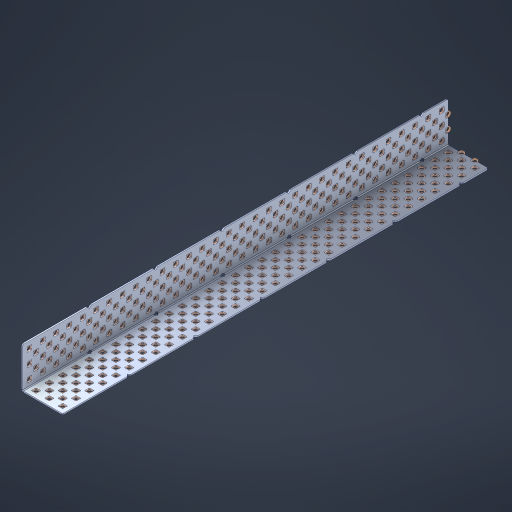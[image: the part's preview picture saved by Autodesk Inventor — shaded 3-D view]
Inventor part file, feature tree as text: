
AUTODESK INVENTOR PART (.ipt)
format: ipt  version: 2023 (Build 270158000, 158)  size: 3,180,544 bytes
history: native  units: in
note: dims shown in document units (in); Inventor stores cm internally (conversion verified against a paired STEP export)
features: other x326, extrude x318, sheet_metal_op x8, sketch x7, pattern_linear x3, mirror x1, chamfer x1
ambient origin geometry x8: Origin, YZ Plane, XZ Plane, XY Plane, X Axis, Y Axis, Z Axis, Center Point
bodies: Solid1 (feature_tree), Body (feature_tree)
feature tree (664):
  sheet_metal_op  "Flanges"
  sheet_metal_op  "Body Pattern"
  pattern_linear  "Center Double"  Spacing1=1.5in  [1 undecoded]
  pattern_linear  "Center Pattern"  Spacing1=0.1875in  [1 undecoded]
  other  "Arc Length"
  pattern_linear  "Notch Pattern"  Spacing1=0.0469in  [1 undecoded]
  other  "Diagonal Plane"
  mirror  "Everything Mirrored"
  chamfer  "End Chamfer"
  sketch  "Sketch1"  dims[d0=1.5in]
  other  "Plate1"
  sketch  "Sketch2"  dims[d1=16.0in]
  other  "Plate2"
  sheet_metal_op  "Bend1"
  sheet_metal_op  "Corner1"
  sketch  "Sketch8"  dims[d2=0.0469in]
  sketch  "Sketch9"  dims[d3=0.0469in]
  other  "Srf91"
  sheet_metal_op  "Body Pattern Sketch"
  other  "Srf92"
  sketch  "Sketch13"  dims[d4=0.0234in]
  sketch  "Sketch15"  dims[d5=0.0938in]
  sketch  "Sketch16"  dims[d6=0.0469in d7=1.5in d8=90.0deg d9=0.0312in d10=0.1875in d11=0.0469in d12=0.0469in d49=0.182in d50=0.02in d52=0.25in d53=0.0469in d54=0.0in d55=0.172in d56=1.0in d57=0.0in d85=0.1473in d86=0.1659in d89=0.0469in d90=0.0in d91=0.04in d92=0.0491in d95=2.5in d96=0.04in d97=0.25in d98=45.0deg d106=0.182in d107=0.02in d110=0.0469in d111=0.0in d112=0.172in d113=0.5in d114=0.0in d117=0.5in d126=0.0491in d127=0.1227in d128=0.08in d129=0.04in d130=2.5in d131=0.25in d132=12.5984in d134=0.5in d135=1.1811in d137=0.5in d140=0.5in d141=1.0in d142=0.3937in d144=0.5in d145=0.071in d146=0.7874in d148=0.5in]
  other  "Srf786"
  other  "Srf856"
  other  "Srf889"
  other  "Srf890"
  other  "Srf891"
  other  "Srf1275"
  other  "Srf1276"
  other  "Srf1278"
  other  "Srf1277"
  other  "Srf1285"
  other  "Srf1286"
  other  "Srf1287"
  other  "Srf1445"
  other  "Srf1446"
  other  "Srf1447"
  other  "Srf1448"
  other  "Srf1449"
  other  "Srf1537"
  other  "Srf1538"
  other  "Srf1539"
  other  "Srf1540"
  other  "Srf1541"
  other  "Srf1807"
  other  "Srf1808"
  other  "Srf1809"
  other  "Srf1810"
  other  "Srf1811"
  other  "Srf1812"
  other  "Srf1813"
  other  "Srf1814"
  other  "Srf1815"
  other  "Srf1816"
  other  "Srf1817"
  other  "Srf1818"
  other  "Srf1819"
  other  "Srf1820"
  other  "Srf1821"
  other  "Srf1822"
  other  "Srf1823"
  other  "Srf1824"
  other  "Srf1825"
  other  "Srf1826"
  other  "Srf1827"
  other  "Srf1828"
  other  "Srf1829"
  other  "Srf1959"
  other  "Srf1960"
  other  "Srf1961"
  other  "Srf1962"
  other  "Srf1963"
  other  "Srf1964"
  other  "Srf1965"
  other  "Srf1966"
  other  "Srf1967"
  other  "Srf1968"
  other  "Srf1969"
  other  "Srf1970"
  other  "Srf1971"
  other  "Srf1972"
  other  "Srf1973"
  other  "Srf1974"
  other  "Srf1975"
  other  "Srf1976"
  other  "Srf1977"
  other  "Srf1978"
  other  "Srf1979"
  other  "Srf1980"
  other  "Srf1981"
  other  "Srf2009"
  other  "Srf2010"
  other  "Srf2011"
  other  "Srf2012"
  other  "Srf2013"
  other  "Srf2014"
  other  "Srf2015"
  other  "Srf2016"
  other  "Srf2017"
  other  "Srf2018"
  other  "Srf2019"
  other  "Srf2020"
  other  "Srf2021"
  other  "Srf2022"
  other  "Srf2023"
  other  "Srf2024"
  other  "Srf2025"
  other  "Srf2026"
  other  "Srf2027"
  other  "Srf2028"
  other  "Srf2029"
  other  "Srf2030"
  other  "Srf2031"
  other  "Srf2032"
  other  "Srf2033"
  other  "Srf2034"
  other  "Srf2035"
  other  "Srf2036"
  other  "Srf2037"
  other  "Srf2038"
  other  "Srf2039"
  other  "Srf2040"
  other  "Srf2043"
  other  "Srf2044"
  other  "Srf2045"
  other  "Srf2046"
  other  "Srf2047"
  other  "Srf2048"
  other  "Srf2049"
  other  "Srf2050"
  other  "Srf2051"
  other  "Srf2052"
  other  "Srf2053"
  other  "Srf2054"
  other  "Srf2055"
  other  "Srf2056"
  other  "Srf2057"
  other  "Srf2058"
  other  "Srf2059"
  other  "Srf2060"
  other  "Srf2061"
  other  "Srf2062"
  other  "Srf2063"
  other  "Srf2064"
  other  "Srf2065"
  other  "Srf2066"
  other  "Srf2067"
  other  "Srf2068"
  other  "Srf2069"
  other  "Srf2070"
  other  "Srf2071"
  other  "Srf2072"
  other  "Srf2073"
  other  "Srf2076"
  other  "Srf2077"
  other  "Srf2078"
  other  "Srf2079"
  other  "Srf2080"
  other  "Srf2081"
  other  "Srf2082"
  other  "Srf2083"
  other  "Srf2084"
  other  "Srf2085"
  other  "Srf2086"
  other  "Srf2087"
  other  "Srf2088"
  other  "Srf2089"
  other  "Srf2090"
  other  "Srf2091"
  other  "Srf2092"
  other  "Srf2093"
  other  "Srf2094"
  other  "Srf2095"
  other  "Srf2096"
  other  "Srf2097"
  other  "Srf2098"
  other  "Srf2099"
  other  "Srf2100"
  other  "Srf2101"
  other  "Srf2102"
  other  "Srf2103"
  other  "Srf2104"
  other  "Srf2105"
  other  "Srf2106"
  other  "Srf2107"
  other  "Srf2108"
  other  "Srf2109"
  other  "Srf2110"
  other  "Srf2111"
  other  "Srf2112"
  other  "Srf2113"
  other  "Srf2114"
  other  "Srf2115"
  other  "Srf2116"
  other  "Srf2117"
  other  "Srf2118"
  other  "Srf2119"
  other  "Srf2120"
  other  "Srf2121"
  other  "Srf2122"
  other  "Srf2123"
  other  "Srf2124"
  other  "Srf2125"
  other  "Srf2126"
  other  "Srf2127"
  other  "Srf2128"
  other  "Srf2129"
  other  "Srf2130"
  other  "Srf2131"
  other  "Srf2132"
  other  "Srf2133"
  other  "Srf2134"
  other  "Srf2135"
  other  "Srf2136"
  other  "Srf2137"
  other  "Srf2138"
  other  "Srf2139"
  other  "Srf2140"
  other  "Srf2141"
  other  "Srf2142"
  other  "Srf2143"
  other  "Srf2144"
  other  "Srf2145"
  other  "Srf2146"
  other  "Srf2147"
  other  "Srf2148"
  other  "Srf2149"
  other  "Srf2150"
  other  "Srf2151"
  other  "Srf2152"
  other  "Srf2153"
  other  "Srf2154"
  other  "Srf2155"
  other  "Srf2156"
  other  "Srf2157"
  other  "Srf2158"
  other  "Srf2159"
  other  "Srf2160"
  other  "Srf2161"
  other  "Srf2162"
  other  "Srf2163"
  other  "Srf2164"
  other  "Srf2165"
  other  "Srf2166"
  other  "Srf2167"
  other  "Srf2168"
  other  "Srf2169"
  other  "Srf2179"
  other  "Srf2180"
  other  "Srf2181"
  other  "Srf2182"
  other  "Srf2183"
  other  "Srf2184"
  other  "Srf2185"
  other  "Srf2186"
  other  "Srf2187"
  other  "Srf2188"
  other  "Srf2189"
  other  "Srf2190"
  other  "Srf2191"
  other  "Srf2192"
  other  "Srf2193"
  other  "Srf2194"
  other  "Srf2195"
  other  "Srf2196"
  other  "Srf2197"
  other  "Srf2198"
  other  "Srf2199"
  other  "Srf2200"
  other  "Srf2201"
  other  "Srf2202"
  other  "Srf2203"
  other  "Srf2204"
  other  "Srf2205"
  other  "Srf2206"
  other  "Srf2207"
  other  "Srf2208"
  other  "Srf2209"
  other  "Srf2210"
  other  "Srf2211"
  other  "Srf2212"
  other  "Srf2213"
  other  "Srf2214"
  other  "Srf2215"
  other  "Srf2216"
  other  "Srf2217"
  other  "Srf2218"
  other  "Srf2219"
  other  "Srf2220"
  other  "Srf2221"
  other  "Srf2222"
  other  "Srf2223"
  other  "Srf2224"
  other  "Srf2225"
  other  "Srf2226"
  other  "Srf2227"
  other  "Srf2228"
  other  "Srf2229"
  other  "Srf2230"
  other  "Srf2231"
  other  "Srf2232"
  other  "Srf2233"
  other  "Srf2234"
  other  "Srf2235"
  other  "Srf2236"
  other  "Srf2237"
  other  "Srf2238"
  other  "Srf2239"
  other  "Srf2240"
  other  "Srf2241"
  other  "Srf2242"
  other  "Srf2243"
  other  "Srf2244"
  other  "Srf2245"
  other  "Srf2246"
  other  "Srf2247"
  other  "Srf2248"
  other  "Srf2249"
  other  "Srf2250"
  other  "Srf2251"
  other  "Srf2252"
  other  "Srf2253"
  other  "Srf2254"
  other  "Srf2255"
  other  "Srf2256"
  other  "Srf2257"
  other  "Srf2258"
  other  "Srf2259"
  other  "Srf2260"
  other  "Srf2261"
  other  "Srf2262"
  other  "Srf2263"
  other  "Srf2264"
  other  "Srf2265"
  other  "Srf2266"
  other  "Srf2267"
  other  "Srf2268"
  other  "Srf2269"
  other  "Srf2270"
  other  "Srf2271"
  sheet_metal_op  "Body Stamp"
  sheet_metal_op  "Body Circle"
  other  "Center Stamp"
  other  "Center Circle"
  sheet_metal_op  "Notch"
  extrude  "ExtrusionSrf92"  Depth=0.0469in
  extrude  "ExtrusionSrf856"  Depth=0.182in
  extrude  "ExtrusionSrf889"  Depth=0.02in
  extrude  "ExtrusionSrf890"  Depth=0.25in
  extrude  "ExtrusionSrf891"  Depth=0.0469in
  extrude  "ExtrusionSrf1275"  TaperAngle=0.0deg  [1 undecoded]
  extrude  "ExtrusionSrf1276"  Depth=0.5in
  extrude  "ExtrusionSrf1277"  Depth=1.0in TaperAngle=0.0deg
  extrude  "ExtrusionSrf1345"  Depth=0.5in
  extrude  "ExtrusionSrf1346"  Depth=0.5in
  extrude  "ExtrusionSrf1347"  Depth=0.0469in
  extrude  "ExtrusionSrf1348"  Depth=0.5in TaperAngle=0.0deg
  extrude  "ExtrusionSrf1445"  Depth=0.5in
  extrude  "ExtrusionSrf1446"  Depth=0.25in TaperAngle=45.0deg
  extrude  "ExtrusionSrf1447"  Depth=0.182in
  extrude  "ExtrusionSrf1448"  Depth=0.02in
  extrude  "ExtrusionSrf1449"  Depth=0.0469in
  extrude  "ExtrusionSrf1537"  TaperAngle=0.0deg  [1 undecoded]
  extrude  "ExtrusionSrf1538"  Depth=0.5in
  extrude  "ExtrusionSrf1539"  Depth=0.5in TaperAngle=0.0deg
  extrude  "ExtrusionSrf1540"  Depth=0.5in
  extrude  "ExtrusionSrf1541"  Depth=0.5in
  extrude  "ExtrusionSrf1807"  Depth=0.5in
  extrude  "ExtrusionSrf1808"  Depth=0.5in
  extrude  "ExtrusionSrf1809"  Depth=0.5in
  extrude  "ExtrusionSrf1810"  Depth=0.5in
  extrude  "ExtrusionSrf1811"  Depth=0.25in
  extrude  "ExtrusionSrf1812"  Depth=0.5in
  extrude  "ExtrusionSrf1813"  Depth=0.5in
  extrude  "ExtrusionSrf1814"  Depth=0.5in
  extrude  "ExtrusionSrf1815"  Depth=1.0in
  extrude  "ExtrusionSrf1816"  Depth=0.3937in
  extrude  "ExtrusionSrf1817"  Depth=0.5in
  extrude  "ExtrusionSrf1818"  Depth=0.5in
  extrude  "ExtrusionSrf1819"  [1 undecoded]
  extrude  "ExtrusionSrf1820"  [1 undecoded]
  extrude  "ExtrusionSrf1821"  [1 undecoded]
  extrude  "ExtrusionSrf1822"  [1 undecoded]
  extrude  "ExtrusionSrf1823"  [1 undecoded]
  extrude  "ExtrusionSrf1824"  [1 undecoded]
  extrude  "ExtrusionSrf1825"  [1 undecoded]
  extrude  "ExtrusionSrf1826"  [1 undecoded]
  extrude  "ExtrusionSrf1827"  [1 undecoded]
  extrude  "ExtrusionSrf1828"  [1 undecoded]
  extrude  "ExtrusionSrf1829"  [1 undecoded]
  extrude  "ExtrusionSrf1959"  [1 undecoded]
  extrude  "ExtrusionSrf1960"  [1 undecoded]
  extrude  "ExtrusionSrf1961"  [1 undecoded]
  extrude  "ExtrusionSrf1962"  [1 undecoded]
  extrude  "ExtrusionSrf1963"  [1 undecoded]
  extrude  "ExtrusionSrf1964"  [1 undecoded]
  extrude  "ExtrusionSrf1965"  [1 undecoded]
  extrude  "ExtrusionSrf1966"  [1 undecoded]
  extrude  "ExtrusionSrf1967"  [1 undecoded]
  extrude  "ExtrusionSrf1968"  [1 undecoded]
  extrude  "ExtrusionSrf1969"  [1 undecoded]
  extrude  "ExtrusionSrf1970"  [1 undecoded]
  extrude  "ExtrusionSrf1971"  [1 undecoded]
  extrude  "ExtrusionSrf1972"  [1 undecoded]
  extrude  "ExtrusionSrf1973"  [1 undecoded]
  extrude  "ExtrusionSrf1974"  [1 undecoded]
  extrude  "ExtrusionSrf1975"  [1 undecoded]
  extrude  "ExtrusionSrf1976"  [1 undecoded]
  extrude  "ExtrusionSrf1977"  [1 undecoded]
  extrude  "ExtrusionSrf1978"  [1 undecoded]
  extrude  "ExtrusionSrf1979"  [1 undecoded]
  extrude  "ExtrusionSrf1980"  [1 undecoded]
  extrude  "ExtrusionSrf1981"  [1 undecoded]
  extrude  "ExtrusionSrf2009"  [1 undecoded]
  extrude  "ExtrusionSrf2010"  [1 undecoded]
  extrude  "ExtrusionSrf2011"  [1 undecoded]
  extrude  "ExtrusionSrf2012"  [1 undecoded]
  extrude  "ExtrusionSrf2013"  [1 undecoded]
  extrude  "ExtrusionSrf2014"  [1 undecoded]
  extrude  "ExtrusionSrf2015"  [1 undecoded]
  extrude  "ExtrusionSrf2016"  [1 undecoded]
  extrude  "ExtrusionSrf2017"  [1 undecoded]
  extrude  "ExtrusionSrf2018"  [1 undecoded]
  extrude  "ExtrusionSrf2019"  [1 undecoded]
  extrude  "ExtrusionSrf2020"  [1 undecoded]
  extrude  "ExtrusionSrf2021"  [1 undecoded]
  extrude  "ExtrusionSrf2022"  [1 undecoded]
  extrude  "ExtrusionSrf2023"  [1 undecoded]
  extrude  "ExtrusionSrf2024"  [1 undecoded]
  extrude  "ExtrusionSrf2025"  [1 undecoded]
  extrude  "ExtrusionSrf2026"  [1 undecoded]
  extrude  "ExtrusionSrf2027"  [1 undecoded]
  extrude  "ExtrusionSrf2028"  [1 undecoded]
  extrude  "ExtrusionSrf2029"  [1 undecoded]
  extrude  "ExtrusionSrf2030"  [1 undecoded]
  extrude  "ExtrusionSrf2031"  [1 undecoded]
  extrude  "ExtrusionSrf2032"  [1 undecoded]
  extrude  "ExtrusionSrf2033"  [1 undecoded]
  extrude  "ExtrusionSrf2034"  [1 undecoded]
  extrude  "ExtrusionSrf2035"  [1 undecoded]
  extrude  "ExtrusionSrf2036"  [1 undecoded]
  extrude  "ExtrusionSrf2037"  [1 undecoded]
  extrude  "ExtrusionSrf2038"  [1 undecoded]
  extrude  "ExtrusionSrf2039"  [1 undecoded]
  extrude  "ExtrusionSrf2040"  [1 undecoded]
  extrude  "ExtrusionSrf2043"  [1 undecoded]
  extrude  "ExtrusionSrf2044"  [1 undecoded]
  extrude  "ExtrusionSrf2045"  [1 undecoded]
  extrude  "ExtrusionSrf2046"  [1 undecoded]
  extrude  "ExtrusionSrf2047"  [1 undecoded]
  extrude  "ExtrusionSrf2048"  [1 undecoded]
  extrude  "ExtrusionSrf2049"  [1 undecoded]
  extrude  "ExtrusionSrf2050"  [1 undecoded]
  extrude  "ExtrusionSrf2051"  [1 undecoded]
  extrude  "ExtrusionSrf2052"  [1 undecoded]
  extrude  "ExtrusionSrf2053"  [1 undecoded]
  extrude  "ExtrusionSrf2054"  [1 undecoded]
  extrude  "ExtrusionSrf2055"  [1 undecoded]
  extrude  "ExtrusionSrf2056"  [1 undecoded]
  extrude  "ExtrusionSrf2057"  [1 undecoded]
  extrude  "ExtrusionSrf2058"  [1 undecoded]
  extrude  "ExtrusionSrf2059"  [1 undecoded]
  extrude  "ExtrusionSrf2060"  [1 undecoded]
  extrude  "ExtrusionSrf2061"  [1 undecoded]
  extrude  "ExtrusionSrf2062"  [1 undecoded]
  extrude  "ExtrusionSrf2063"  [1 undecoded]
  extrude  "ExtrusionSrf2064"  [1 undecoded]
  extrude  "ExtrusionSrf2065"  [1 undecoded]
  extrude  "ExtrusionSrf2066"  [1 undecoded]
  extrude  "ExtrusionSrf2067"  [1 undecoded]
  extrude  "ExtrusionSrf2068"  [1 undecoded]
  extrude  "ExtrusionSrf2069"  [1 undecoded]
  extrude  "ExtrusionSrf2070"  [1 undecoded]
  extrude  "ExtrusionSrf2071"  [1 undecoded]
  extrude  "ExtrusionSrf2072"  [1 undecoded]
  extrude  "ExtrusionSrf2073"  [1 undecoded]
  extrude  "ExtrusionSrf2076"  [1 undecoded]
  extrude  "ExtrusionSrf2077"  [1 undecoded]
  extrude  "ExtrusionSrf2078"  [1 undecoded]
  extrude  "ExtrusionSrf2079"  [1 undecoded]
  extrude  "ExtrusionSrf2080"  [1 undecoded]
  extrude  "ExtrusionSrf2081"  [1 undecoded]
  extrude  "ExtrusionSrf2082"  [1 undecoded]
  extrude  "ExtrusionSrf2083"  [1 undecoded]
  extrude  "ExtrusionSrf2084"  [1 undecoded]
  extrude  "ExtrusionSrf2085"  [1 undecoded]
  extrude  "ExtrusionSrf2086"  [1 undecoded]
  extrude  "ExtrusionSrf2087"  [1 undecoded]
  extrude  "ExtrusionSrf2088"  [1 undecoded]
  extrude  "ExtrusionSrf2089"  [1 undecoded]
  extrude  "ExtrusionSrf2090"  [1 undecoded]
  extrude  "ExtrusionSrf2091"  [1 undecoded]
  extrude  "ExtrusionSrf2092"  [1 undecoded]
  extrude  "ExtrusionSrf2093"  [1 undecoded]
  extrude  "ExtrusionSrf2094"  [1 undecoded]
  extrude  "ExtrusionSrf2095"  [1 undecoded]
  extrude  "ExtrusionSrf2096"  [1 undecoded]
  extrude  "ExtrusionSrf2097"  [1 undecoded]
  extrude  "ExtrusionSrf2098"  [1 undecoded]
  extrude  "ExtrusionSrf2099"  [1 undecoded]
  extrude  "ExtrusionSrf2100"  [1 undecoded]
  extrude  "ExtrusionSrf2101"  [1 undecoded]
  extrude  "ExtrusionSrf2102"  [1 undecoded]
  extrude  "ExtrusionSrf2103"  [1 undecoded]
  extrude  "ExtrusionSrf2104"  [1 undecoded]
  extrude  "ExtrusionSrf2105"  [1 undecoded]
  extrude  "ExtrusionSrf2106"  [1 undecoded]
  extrude  "ExtrusionSrf2107"  [1 undecoded]
  extrude  "ExtrusionSrf2108"  [1 undecoded]
  extrude  "ExtrusionSrf2109"  [1 undecoded]
  extrude  "ExtrusionSrf2110"  [1 undecoded]
  extrude  "ExtrusionSrf2111"  [1 undecoded]
  extrude  "ExtrusionSrf2112"  [1 undecoded]
  extrude  "ExtrusionSrf2113"  [1 undecoded]
  extrude  "ExtrusionSrf2114"  [1 undecoded]
  extrude  "ExtrusionSrf2115"  [1 undecoded]
  extrude  "ExtrusionSrf2116"  [1 undecoded]
  extrude  "ExtrusionSrf2117"  [1 undecoded]
  extrude  "ExtrusionSrf2118"  [1 undecoded]
  extrude  "ExtrusionSrf2119"  [1 undecoded]
  extrude  "ExtrusionSrf2120"  [1 undecoded]
  extrude  "ExtrusionSrf2121"  [1 undecoded]
  extrude  "ExtrusionSrf2122"  [1 undecoded]
  extrude  "ExtrusionSrf2123"  [1 undecoded]
  extrude  "ExtrusionSrf2124"  [1 undecoded]
  extrude  "ExtrusionSrf2125"  [1 undecoded]
  extrude  "ExtrusionSrf2126"  [1 undecoded]
  extrude  "ExtrusionSrf2127"  [1 undecoded]
  extrude  "ExtrusionSrf2128"  [1 undecoded]
  extrude  "ExtrusionSrf2129"  [1 undecoded]
  extrude  "ExtrusionSrf2130"  [1 undecoded]
  extrude  "ExtrusionSrf2131"  [1 undecoded]
  extrude  "ExtrusionSrf2132"  [1 undecoded]
  extrude  "ExtrusionSrf2133"  [1 undecoded]
  extrude  "ExtrusionSrf2134"  [1 undecoded]
  extrude  "ExtrusionSrf2135"  [1 undecoded]
  extrude  "ExtrusionSrf2136"  [1 undecoded]
  extrude  "ExtrusionSrf2137"  [1 undecoded]
  extrude  "ExtrusionSrf2138"  [1 undecoded]
  extrude  "ExtrusionSrf2139"  [1 undecoded]
  extrude  "ExtrusionSrf2140"  [1 undecoded]
  extrude  "ExtrusionSrf2141"  [1 undecoded]
  extrude  "ExtrusionSrf2142"  [1 undecoded]
  extrude  "ExtrusionSrf2143"  [1 undecoded]
  extrude  "ExtrusionSrf2144"  [1 undecoded]
  extrude  "ExtrusionSrf2145"  [1 undecoded]
  extrude  "ExtrusionSrf2146"  [1 undecoded]
  extrude  "ExtrusionSrf2147"  [1 undecoded]
  extrude  "ExtrusionSrf2148"  [1 undecoded]
  extrude  "ExtrusionSrf2149"  [1 undecoded]
  extrude  "ExtrusionSrf2150"  [1 undecoded]
  extrude  "ExtrusionSrf2151"  [1 undecoded]
  extrude  "ExtrusionSrf2152"  [1 undecoded]
  extrude  "ExtrusionSrf2153"  [1 undecoded]
  extrude  "ExtrusionSrf2154"  [1 undecoded]
  extrude  "ExtrusionSrf2155"  [1 undecoded]
  extrude  "ExtrusionSrf2156"  [1 undecoded]
  extrude  "ExtrusionSrf2157"  [1 undecoded]
  extrude  "ExtrusionSrf2158"  [1 undecoded]
  extrude  "ExtrusionSrf2159"  [1 undecoded]
  extrude  "ExtrusionSrf2160"  [1 undecoded]
  extrude  "ExtrusionSrf2161"  [1 undecoded]
  extrude  "ExtrusionSrf2162"  [1 undecoded]
  extrude  "ExtrusionSrf2163"  [1 undecoded]
  extrude  "ExtrusionSrf2164"  [1 undecoded]
  extrude  "ExtrusionSrf2165"  [1 undecoded]
  extrude  "ExtrusionSrf2166"  [1 undecoded]
  extrude  "ExtrusionSrf2167"  [1 undecoded]
  extrude  "ExtrusionSrf2168"  [1 undecoded]
  extrude  "ExtrusionSrf2169"  [1 undecoded]
  extrude  "ExtrusionSrf2179"  [1 undecoded]
  extrude  "ExtrusionSrf2180"  [1 undecoded]
  extrude  "ExtrusionSrf2181"  [1 undecoded]
  extrude  "ExtrusionSrf2182"  [1 undecoded]
  extrude  "ExtrusionSrf2183"  [1 undecoded]
  extrude  "ExtrusionSrf2184"  [1 undecoded]
  extrude  "ExtrusionSrf2185"  [1 undecoded]
  extrude  "ExtrusionSrf2186"  [1 undecoded]
  extrude  "ExtrusionSrf2187"  [1 undecoded]
  extrude  "ExtrusionSrf2188"  [1 undecoded]
  extrude  "ExtrusionSrf2189"  [1 undecoded]
  extrude  "ExtrusionSrf2190"  [1 undecoded]
  extrude  "ExtrusionSrf2191"  [1 undecoded]
  extrude  "ExtrusionSrf2192"  [1 undecoded]
  extrude  "ExtrusionSrf2193"  [1 undecoded]
  extrude  "ExtrusionSrf2194"  [1 undecoded]
  extrude  "ExtrusionSrf2195"  [1 undecoded]
  extrude  "ExtrusionSrf2196"  [1 undecoded]
  extrude  "ExtrusionSrf2197"  [1 undecoded]
  extrude  "ExtrusionSrf2198"  [1 undecoded]
  extrude  "ExtrusionSrf2199"  [1 undecoded]
  extrude  "ExtrusionSrf2200"  [1 undecoded]
  extrude  "ExtrusionSrf2201"  [1 undecoded]
  extrude  "ExtrusionSrf2202"  [1 undecoded]
  extrude  "ExtrusionSrf2203"  [1 undecoded]
  extrude  "ExtrusionSrf2204"  [1 undecoded]
  extrude  "ExtrusionSrf2205"  [1 undecoded]
  extrude  "ExtrusionSrf2206"  [1 undecoded]
  extrude  "ExtrusionSrf2207"  [1 undecoded]
  extrude  "ExtrusionSrf2208"  [1 undecoded]
  extrude  "ExtrusionSrf2209"  [1 undecoded]
  extrude  "ExtrusionSrf2210"  [1 undecoded]
  extrude  "ExtrusionSrf2211"  [1 undecoded]
  extrude  "ExtrusionSrf2212"  [1 undecoded]
  extrude  "ExtrusionSrf2213"  [1 undecoded]
  extrude  "ExtrusionSrf2214"  [1 undecoded]
  extrude  "ExtrusionSrf2215"  [1 undecoded]
  extrude  "ExtrusionSrf2216"  [1 undecoded]
  extrude  "ExtrusionSrf2217"  [1 undecoded]
  extrude  "ExtrusionSrf2218"  [1 undecoded]
  extrude  "ExtrusionSrf2219"  [1 undecoded]
  extrude  "ExtrusionSrf2220"  [1 undecoded]
  extrude  "ExtrusionSrf2221"  [1 undecoded]
  extrude  "ExtrusionSrf2222"  [1 undecoded]
  extrude  "ExtrusionSrf2223"  [1 undecoded]
  extrude  "ExtrusionSrf2224"  [1 undecoded]
  extrude  "ExtrusionSrf2225"  [1 undecoded]
  extrude  "ExtrusionSrf2226"  [1 undecoded]
  extrude  "ExtrusionSrf2227"  [1 undecoded]
  extrude  "ExtrusionSrf2228"  [1 undecoded]
  extrude  "ExtrusionSrf2229"  [1 undecoded]
  extrude  "ExtrusionSrf2230"  [1 undecoded]
  extrude  "ExtrusionSrf2231"  [1 undecoded]
  extrude  "ExtrusionSrf2232"  [1 undecoded]
  extrude  "ExtrusionSrf2233"  [1 undecoded]
  extrude  "ExtrusionSrf2234"  [1 undecoded]
  extrude  "ExtrusionSrf2235"  [1 undecoded]
  extrude  "ExtrusionSrf2236"  [1 undecoded]
  extrude  "ExtrusionSrf2237"  [1 undecoded]
  extrude  "ExtrusionSrf2238"  [1 undecoded]
  extrude  "ExtrusionSrf2239"  [1 undecoded]
  extrude  "ExtrusionSrf2240"  [1 undecoded]
  extrude  "ExtrusionSrf2241"  [1 undecoded]
  extrude  "ExtrusionSrf2242"  [1 undecoded]
  extrude  "ExtrusionSrf2243"  [1 undecoded]
  extrude  "ExtrusionSrf2244"  [1 undecoded]
  extrude  "ExtrusionSrf2245"  [1 undecoded]
  extrude  "ExtrusionSrf2246"  [1 undecoded]
  extrude  "ExtrusionSrf2247"  [1 undecoded]
  extrude  "ExtrusionSrf2248"  [1 undecoded]
  extrude  "ExtrusionSrf2249"  [1 undecoded]
  extrude  "ExtrusionSrf2250"  [1 undecoded]
  extrude  "ExtrusionSrf2251"  [1 undecoded]
  extrude  "ExtrusionSrf2252"  [1 undecoded]
  extrude  "ExtrusionSrf2253"  [1 undecoded]
  extrude  "ExtrusionSrf2254"  [1 undecoded]
  extrude  "ExtrusionSrf2255"  [1 undecoded]
  extrude  "ExtrusionSrf2256"  [1 undecoded]
  extrude  "ExtrusionSrf2257"  [1 undecoded]
  extrude  "ExtrusionSrf2258"  [1 undecoded]
  extrude  "ExtrusionSrf2259"  [1 undecoded]
  extrude  "ExtrusionSrf2260"  [1 undecoded]
  extrude  "ExtrusionSrf2261"  [1 undecoded]
  extrude  "ExtrusionSrf2262"  [1 undecoded]
  extrude  "ExtrusionSrf2263"  [1 undecoded]
  extrude  "ExtrusionSrf2264"  [1 undecoded]
  extrude  "ExtrusionSrf2265"  [1 undecoded]
  extrude  "ExtrusionSrf2266"  [1 undecoded]
  extrude  "ExtrusionSrf2267"  [1 undecoded]
  extrude  "ExtrusionSrf2268"  [1 undecoded]
  extrude  "ExtrusionSrf2269"  [1 undecoded]
  extrude  "ExtrusionSrf2270"  [1 undecoded]
  extrude  "ExtrusionSrf2271"  [1 undecoded]
note: 289 required parameter values undecoded (feature->parameter linkage not recoverable at this tier; creation-order binding heuristic only, values carry confidence <= 0.55)
